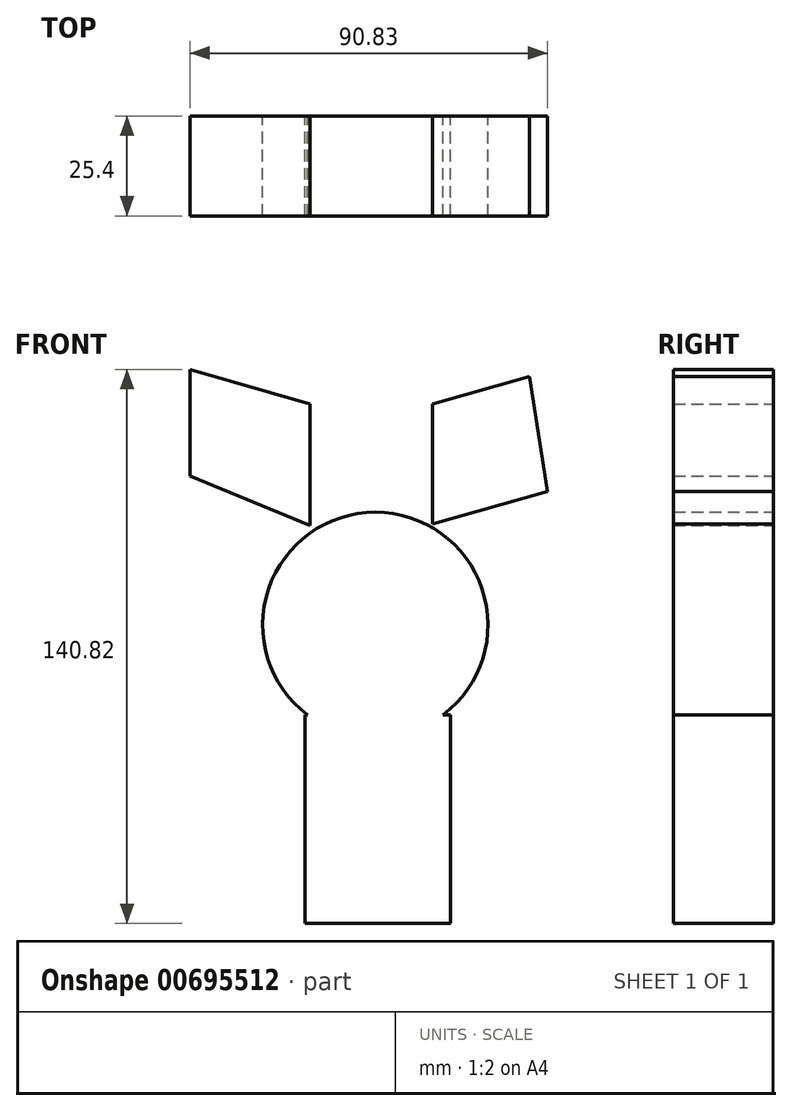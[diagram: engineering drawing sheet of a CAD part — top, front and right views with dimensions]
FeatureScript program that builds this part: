
annotation { "Feature Type Name" : "Feature", "Feature Type Description" : "" }
export const myFeature = defineFeature(function(context is Context, id is Id, definition is map)
    precondition{}
    {
        {
            var Q0;
            Q0=qCreatedBy(makeId("Front.planeOp"),FACE);
            var sketch = newSketch(context, id + "F0", { "sketchPlane" : qUnion([Q0])});
            skCircle(sketch, "E0", {"center": v(0, 0) * mm, "radius": 28.62 * mm});
            skSolve(sketch);
        }
        {
            var Q0;
            Q0 = qSketchRegion(id + "F0", true);
            extrude(context, id + "F1", {"entities" : qUnion([Q0]), "depth" : 25.4 * mm, "offsetDistance" : 25.4 * mm});
        }
        {
            var Q0;
            Q0=qCreatedBy(makeId("Front.planeOp"),FACE);
            var sketch = newSketch(context, id + "F2", { "sketchPlane" : qUnion([Q0])});
            skLineSegment(sketch, "E1", {"start": v(-16.61, 25.3) * mm, "end": v(-16.61, 56.08) * mm});
            skLineSegment(sketch, "E2", {"start": v(-16.61, 56.08) * mm, "end": v(-47.1, 64.92) * mm});
            skLineSegment(sketch, "E3", {"start": v(-47.1, 64.92) * mm, "end": v(-47.1, 37.8) * mm});
            skLineSegment(sketch, "E4", {"start": v(-47.1, 37.8) * mm, "end": v(-16.61, 25.3) * mm});
            skSolve(sketch);
        }
        {
            var Q0;
            Q0=makeQuery(id+"F2.imprint","IMPRINT",FACE,{"disambiguationData":[TD([[makeQuery(id+"F2.imprint","IMPRINT",EDGE,{"derivedFrom":sQuery(id+"F2.wireOp",EDGE,"E1")}),1.0]])]});
            extrude(context, id + "F3", {"entities" : qUnion([Q0]), "depth" : 25.4 * mm, "offsetDistance" : 25.4 * mm});
        }
        {
            var Q0;
            Q0=qCreatedBy(makeId("Front.planeOp"),FACE);
            var sketch = newSketch(context, id + "F4", { "sketchPlane" : qUnion([Q0])});
            skLineSegment(sketch, "E5", {"start": v(14.48, 25.6) * mm, "end": v(14.48, 56.08) * mm});
            skLineSegment(sketch, "E6", {"start": v(14.48, 56.08) * mm, "end": v(39.17, 63.1) * mm});
            skLineSegment(sketch, "E7", {"start": v(39.17, 63.1) * mm, "end": v(43.74, 33.83) * mm});
            skLineSegment(sketch, "E8", {"start": v(43.74, 33.83) * mm, "end": v(14.48, 25.6) * mm});
            skSolve(sketch);
        }
        {
            var Q0;
            Q0=makeQuery(id+"F4.imprint","IMPRINT",FACE,{"disambiguationData":[TD([[makeQuery(id+"F4.imprint","IMPRINT",EDGE,{"derivedFrom":sQuery(id+"F4.wireOp",EDGE,"E5")}),-1.0]])]});
            extrude(context, id + "F5", {"entities" : qUnion([Q0]), "depth" : 25.4 * mm, "offsetDistance" : 25.4 * mm});
        }
        {
            var Q0;
            Q0=qCreatedBy(makeId("Front.planeOp"),FACE);
            var sketch = newSketch(context, id + "F6", { "sketchPlane" : qUnion([Q0])});
            skLineSegment(sketch, "E9.bottom", {"start": v(-17.83, -22.86) * mm, "end": v(19.05, -22.86) * mm});
            skLineSegment(sketch, "E9.top", {"start": v(-17.83, -75.9) * mm, "end": v(19.05, -75.9) * mm});
            skLineSegment(sketch, "E9.left", {"start": v(-17.83, -22.86) * mm, "end": v(-17.83, -75.9) * mm});
            skLineSegment(sketch, "E9.right", {"start": v(19.05, -22.86) * mm, "end": v(19.05, -75.9) * mm});
            skSolve(sketch);
        }
        {
            var Q0;
            Q0 = qSketchRegion(id + "F6", true);
            extrude(context, id + "F7", {"entities" : qUnion([Q0]), "operationType" : NewBodyOperationType.ADD, "depth" : 25.4 * mm, "offsetDistance" : 25.4 * mm});
        }
    });
